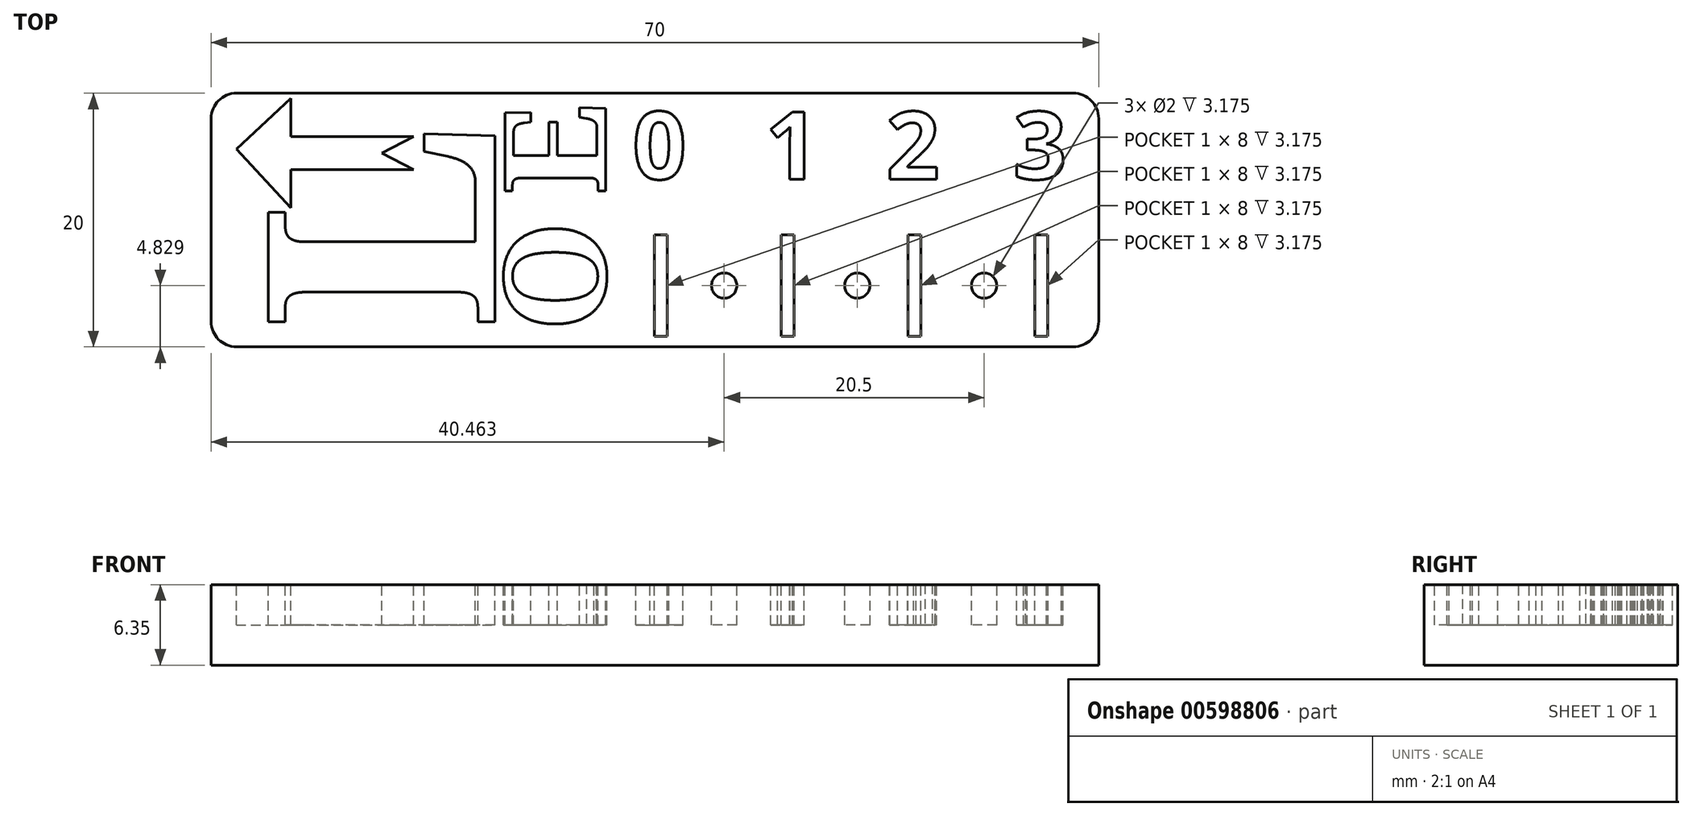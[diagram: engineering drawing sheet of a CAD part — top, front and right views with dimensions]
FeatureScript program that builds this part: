
annotation { "Feature Type Name" : "Feature", "Feature Type Description" : "" }
export const myFeature = defineFeature(function(context is Context, id is Id, definition is map)
    precondition{}
    {
        {
            var Q0;
            Q0=qCreatedBy(makeId("Top.planeOp"),FACE);
            var sketch = newSketch(context, id + "F0", { "sketchPlane" : qUnion([Q0])});
            skLineSegment(sketch, "E0.bottom", {"start": v(-55.27, 9.73) * mm, "end": v(10.73, 9.73) * mm});
            skLineSegment(sketch, "E0.top", {"start": v(-55.27, -10.27) * mm, "end": v(10.73, -10.27) * mm});
            skLineSegment(sketch, "E0.left", {"start": v(-57.27, 7.73) * mm, "end": v(-57.27, -8.27) * mm});
            skLineSegment(sketch, "E0.right", {"start": v(12.73, 7.73) * mm, "end": v(12.73, -8.27) * mm});
            skPoint(sketch, "E1.visualSharp", {"position": v(-57.27, 9.73) * mm});
            skArc(sketch, "E1.filletArc", {"start": v(-55.27, 9.73) * mm, "mid": v(-56.68, 9.15) * mm, "end": v(-57.27, 7.73) * mm});
            skPoint(sketch, "E2.visualSharp", {"position": v(12.73, 9.73) * mm});
            skArc(sketch, "E2.filletArc", {"start": v(12.73, 7.73) * mm, "mid": v(12.14, 9.15) * mm, "end": v(10.73, 9.73) * mm});
            skPoint(sketch, "E3.visualSharp", {"position": v(12.73, -10.27) * mm});
            skArc(sketch, "E3.filletArc", {"start": v(10.73, -10.27) * mm, "mid": v(12.14, -9.68) * mm, "end": v(12.73, -8.27) * mm});
            skPoint(sketch, "E4.visualSharp", {"position": v(-57.27, -10.27) * mm});
            skArc(sketch, "E4.filletArc", {"start": v(-57.27, -8.27) * mm, "mid": v(-56.68, -9.68) * mm, "end": v(-55.27, -10.27) * mm});
            skSolve(sketch);
        }
        {
            var Q0;
            Q0=qSketchRegion(id+"F0",true);
            extrude(context, id + "F1", {"entities" : qUnion([Q0]), "depth" : 6.35 * mm, "offsetDistance" : 25.4 * mm});
        }
        {
            var Q0;
            Q0=makeQuery(id+"F1.opExtrude","CAP_FACE",FACE,{"disambiguationData":[OSD([sQuery(id+"F0.wireOp",EDGE,"E0.bottom"),sQuery(id+"F0.wireOp",EDGE,"E0.top"),sQuery(id+"F0.wireOp",EDGE,"E0.left"),sQuery(id+"F0.wireOp",EDGE,"E0.right")])],"isStart":false});
            var sketch = newSketch(context, id + "F2", { "sketchPlane" : qUnion([Q0])});
            skText(sketch, "E5", { "text": "L", "fontName": "NotoSerif-Bold.ttf"});
            skText(sketch, "E6", { "text": "O\n", "fontName": "NotoSerif-Bold.ttf"});
            skText(sketch, "E7", { "text": "E", "fontName": "NotoSerif-Bold.ttf"});
            skLineSegment(sketch, "E8.bottom", {"start": v(-22.3, -1.44) * mm, "end": v(-21.3, -1.44) * mm});
            skLineSegment(sketch, "E8.top", {"start": v(-22.3, -9.44) * mm, "end": v(-21.3, -9.44) * mm});
            skLineSegment(sketch, "E8.left", {"start": v(-22.3, -1.44) * mm, "end": v(-22.3, -9.44) * mm});
            skLineSegment(sketch, "E8.right", {"start": v(-21.3, -1.44) * mm, "end": v(-21.3, -9.44) * mm});
            skLineSegment(sketch, "E9.bottom", {"start": v(-12.3, -1.44) * mm, "end": v(-11.3, -1.44) * mm});
            skLineSegment(sketch, "E9.top", {"start": v(-12.3, -9.44) * mm, "end": v(-11.3, -9.44) * mm});
            skLineSegment(sketch, "E9.left", {"start": v(-12.3, -1.44) * mm, "end": v(-12.3, -9.44) * mm});
            skLineSegment(sketch, "E9.right", {"start": v(-11.3, -1.44) * mm, "end": v(-11.3, -9.44) * mm});
            skLineSegment(sketch, "E10.bottom", {"start": v(-2.3, -1.44) * mm, "end": v(-1.3, -1.44) * mm});
            skLineSegment(sketch, "E10.top", {"start": v(-2.3, -9.44) * mm, "end": v(-1.3, -9.44) * mm});
            skLineSegment(sketch, "E10.left", {"start": v(-2.3, -1.44) * mm, "end": v(-2.3, -9.44) * mm});
            skLineSegment(sketch, "E10.right", {"start": v(-1.3, -1.44) * mm, "end": v(-1.3, -9.44) * mm});
            skLineSegment(sketch, "E11.bottom", {"start": v(7.7, -1.44) * mm, "end": v(8.7, -1.44) * mm});
            skLineSegment(sketch, "E11.top", {"start": v(7.7, -9.44) * mm, "end": v(8.7, -9.44) * mm});
            skLineSegment(sketch, "E11.left", {"start": v(7.7, -1.44) * mm, "end": v(7.7, -9.44) * mm});
            skLineSegment(sketch, "E11.right", {"start": v(8.7, -1.44) * mm, "end": v(8.7, -9.44) * mm});
            skPoint(sketch, "E12", {"position": v(-21.8, -1.44) * mm});
            skPoint(sketch, "E13", {"position": v(-11.8, -1.44) * mm});
            skPoint(sketch, "E14", {"position": v(-1.8, -1.44) * mm});
            skCircle(sketch, "E15", {"center": v(-16.8, -5.44) * mm, "radius": 1 * mm});
            skPoint(sketch, "E16", {"position": v(-21.3, -5.44) * mm});
            skCircle(sketch, "E17", {"center": v(-6.3, -5.44) * mm, "radius": 1 * mm});
            skCircle(sketch, "E18", {"center": v(3.7, -5.44) * mm, "radius": 1 * mm});
            skPoint(sketch, "E19", {"position": v(-11.3, -5.44) * mm});
            skPoint(sketch, "E20", {"position": v(-1.3, -5.44) * mm});
            skText(sketch, "E21", { "text": "0", "fontName": "OpenSans-Bold.ttf"});
            skText(sketch, "E22", { "text": "1", "fontName": "OpenSans-Bold.ttf"});
            skText(sketch, "E23", { "text": "2", "fontName": "OpenSans-Bold.ttf"});
            skText(sketch, "E24", { "text": "3", "fontName": "OpenSans-Bold.ttf"});
            skLineSegment(sketch, "E25", {"start": v(-41.31, 3.7) * mm, "end": v(-50.98, 3.7) * mm});
            skLineSegment(sketch, "E26", {"start": v(-50.98, 3.7) * mm, "end": v(-50.98, 0.7) * mm});
            skLineSegment(sketch, "E27", {"start": v(-50.98, 0.7) * mm, "end": v(-55.27, 5.33) * mm});
            skLineSegment(sketch, "E28", {"start": v(-55.27, 5.33) * mm, "end": v(-50.98, 9.31) * mm});
            skLineSegment(sketch, "E29", {"start": v(-50.98, 9.31) * mm, "end": v(-50.98, 6.31) * mm});
            skLineSegment(sketch, "E30", {"start": v(-50.98, 6.31) * mm, "end": v(-41.31, 6.31) * mm});
            skPoint(sketch, "E31", {"position": v(-43.8, 5) * mm});
            skLineSegment(sketch, "E32", {"start": v(-43.8, 5) * mm, "end": v(-41.31, 3.7) * mm});
            skLineSegment(sketch, "E33", {"start": v(-43.8, 5) * mm, "end": v(-41.31, 6.31) * mm});
            const initialGuessF2  = {"E5": [-0.0349, -0.00898, 0, 1, 0.018], "E6": [-0.02616, -0.00908, 0, 1, 0.008], "E7": [-0.02616, 0.0017, 0, 1, 0.008], "E21": [-0.02403, 0.00296, 1, 0, 0.00534], "E22": [-0.01358, 0.00296, 1, 0, 0.00534], "E23": [-0.00404, 0.00296, 1, 0, 0.00534], "E24": [0.00598, 0.00296, 1, 0, 0.00534]};
            skSetInitialGuess(sketch, initialGuessF2);
            skSolve(sketch);
        }
        {
            var Q0;
            Q0=qSketchRegion(id+"F2",true);
            extrude(context, id + "F3", {"entities" : qUnion([Q0]), "operationType" : NewBodyOperationType.REMOVE, "oppositeDirection" : true, "depth" : 3.17 * mm, "offsetDistance" : 25.4 * mm});
        }
    });
